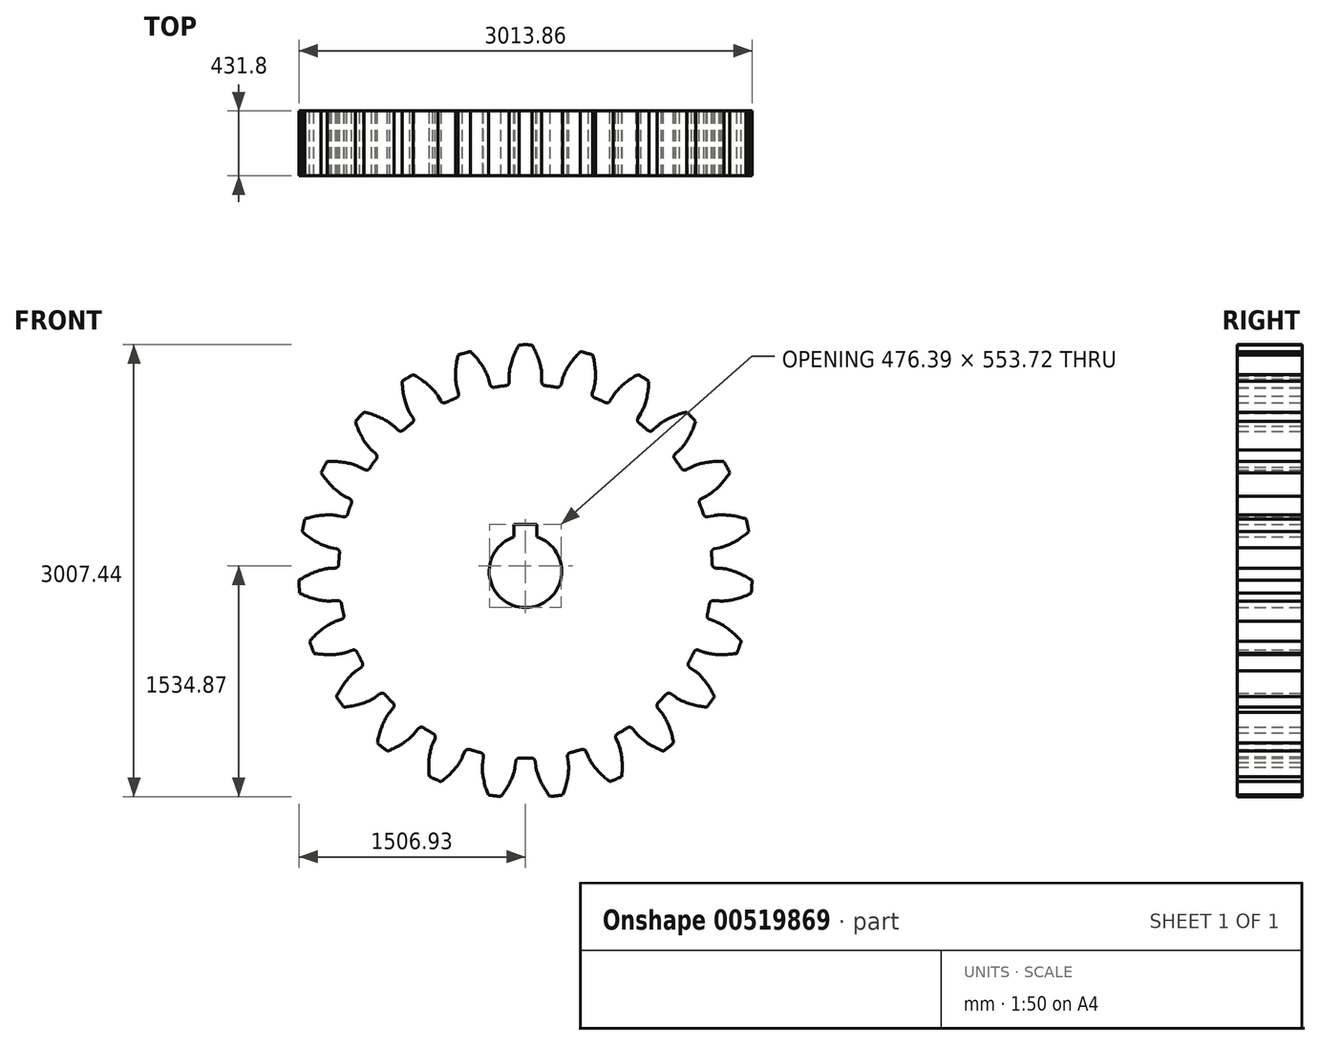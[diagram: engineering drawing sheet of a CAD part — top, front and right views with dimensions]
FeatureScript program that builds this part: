
annotation { "Feature Type Name" : "Feature", "Feature Type Description" : "" }
export const myFeature = defineFeature(function(context is Context, id is Id, definition is map)
    precondition{}
    {
        {
            var Q0;
            Q0=qCreatedBy(makeId("Front.planeOp"),FACE);
            var sketch = newSketch(context, id + "F0", { "sketchPlane" : qUnion([Q0])});
            skCircle(sketch, "E0", {"center": v(0, -4.4) * mm, "radius": 762 * mm});
            skArc(sketch, "E1", {"start": v(-76.2, 224.55) * mm, "mid": v(0, -245.7) * mm, "end": v(76.2, 224.55) * mm});
            skLineSegment(sketch, "E2", {"start": v(-76.2, 224.55) * mm, "end": v(-76.2, 308.01) * mm});
            skLineSegment(sketch, "E3", {"start": v(-76.2, 308.01) * mm, "end": v(76.2, 308.01) * mm});
            skLineSegment(sketch, "E4", {"start": v(76.2, 308.01) * mm, "end": v(76.2, 224.55) * mm});
            skArc(sketch, "E5", {"start": v(169.21, 1226.71) * mm, "mid": v(150.16, 1229.18) * mm, "end": v(131.07, 1231.36) * mm});
            skFitSpline(sketch, "E6", {"points": [v(42.87, 1503.1) * mm, v(49.5, 1490.92) * mm, v(64.07, 1462.34) * mm, v(82.4, 1419.04) * mm, v(96.22, 1376.5) * mm, v(104.12, 1342.62) * mm, v(107.6, 1318.04) * mm, v(108.63, 1303.15) * mm, v(108.4, 1296.54) * mm, v(108.35, 1294.88) * mm]});
            skFitSpline(sketch, "E7", {"points": [v(-42.87, 1503.1) * mm, v(-49.5, 1490.92) * mm, v(-64.07, 1462.34) * mm, v(-82.4, 1419.04) * mm, v(-96.22, 1376.5) * mm, v(-104.12, 1342.62) * mm, v(-107.6, 1318.04) * mm, v(-108.63, 1303.15) * mm, v(-108.4, 1296.54) * mm, v(-108.35, 1294.88) * mm]});
            skLineSegment(sketch, "E8", {"start": v(-108.35, 1294.88) * mm, "end": v(-108.35, 1256.61) * mm});
            skArc(sketch, "E9", {"start": v(-131.07, 1231.36) * mm, "mid": v(-114.87, 1239.63) * mm, "end": v(-108.35, 1256.61) * mm});
            skArc(sketch, "E10", {"start": v(108.35, 1256.61) * mm, "mid": v(114.87, 1239.63) * mm, "end": v(131.07, 1231.36) * mm});
            skLineSegment(sketch, "E11", {"start": v(108.35, 1294.88) * mm, "end": v(108.35, 1256.61) * mm});
            skArc(sketch, "E12", {"start": v(-131.07, 1231.36) * mm, "mid": v(-150.16, 1229.18) * mm, "end": v(-169.21, 1226.71) * mm});
            skArc(sketch, "E13", {"start": v(42.87, 1503.1) * mm, "mid": v(0, 1503.72) * mm, "end": v(-42.87, 1503.1) * mm});
            skFitSpline(sketch, "E14", {"points": [v(-365.44, 1458.77) * mm, v(-355.77, 1448.82) * mm, v(-334.03, 1425.23) * mm, v(-304.7, 1388.48) * mm, v(-279.92, 1351.26) * mm, v(-263.16, 1320.76) * mm, v(-253.19, 1298.03) * mm, v(-248.17, 1283.97) * mm, v(-246.6, 1277.54) * mm, v(-246.2, 1275.94) * mm]});
            skFitSpline(sketch, "E15", {"points": [v(-448, 1435.64) * mm, v(-451.1, 1422.11) * mm, v(-457.42, 1390.66) * mm, v(-463.39, 1344.02) * mm, v(-465.22, 1299.34) * mm, v(-463.69, 1264.58) * mm, v(-460.4, 1239.97) * mm, v(-457.38, 1225.36) * mm, v(-455.38, 1219.05) * mm, v(-454.88, 1217.47) * mm]});
            skLineSegment(sketch, "E16", {"start": v(-454.88, 1217.47) * mm, "end": v(-444.55, 1180.62) * mm});
            skArc(sketch, "E17", {"start": v(-459.62, 1150.17) * mm, "mid": v(-446.25, 1162.5) * mm, "end": v(-444.55, 1180.62) * mm});
            skArc(sketch, "E18", {"start": v(-235.88, 1239.09) * mm, "mid": v(-225.03, 1224.49) * mm, "end": v(-207.2, 1220.9) * mm});
            skLineSegment(sketch, "E19", {"start": v(-246.2, 1275.94) * mm, "end": v(-235.88, 1239.09) * mm});
            skArc(sketch, "E20", {"start": v(-459.62, 1150.17) * mm, "mid": v(-477.41, 1142.92) * mm, "end": v(-495.1, 1135.4) * mm});
            skArc(sketch, "E21", {"start": v(-169.21, 1226.71) * mm, "mid": v(-188.23, 1223.95) * mm, "end": v(-207.2, 1220.9) * mm});
            skArc(sketch, "E22", {"start": v(-365.44, 1458.77) * mm, "mid": v(-406.89, 1447.8) * mm, "end": v(-448, 1435.64) * mm});
            skFitSpline(sketch, "E23", {"points": [v(-746.65, 1305.92) * mm, v(-734.66, 1298.95) * mm, v(-707.35, 1282.1) * mm, v(-669.2, 1254.63) * mm, v(-635.29, 1225.47) * mm, v(-610.93, 1200.62) * mm, v(-595.19, 1181.42) * mm, v(-586.57, 1169.24) * mm, v(-583.32, 1163.47) * mm, v(-582.51, 1162.03) * mm]});
            skFitSpline(sketch, "E24", {"points": [v(-819.9, 1261.37) * mm, v(-819.24, 1247.51) * mm, v(-816.84, 1215.52) * mm, v(-810, 1169) * mm, v(-799.71, 1125.48) * mm, v(-788.86, 1092.42) * mm, v(-779.05, 1069.61) * mm, v(-772.2, 1056.35) * mm, v(-768.58, 1050.82) * mm, v(-767.67, 1049.43) * mm]});
            skLineSegment(sketch, "E25", {"start": v(-767.67, 1049.43) * mm, "end": v(-747.79, 1016.74) * mm});
            skArc(sketch, "E26", {"start": v(-754.07, 983.35) * mm, "mid": v(-744.53, 998.84) * mm, "end": v(-747.79, 1016.74) * mm});
            skArc(sketch, "E27", {"start": v(-562.63, 1129.33) * mm, "mid": v(-548.23, 1118.2) * mm, "end": v(-530.1, 1119.56) * mm});
            skLineSegment(sketch, "E28", {"start": v(-582.51, 1162.03) * mm, "end": v(-562.63, 1129.33) * mm});
            skArc(sketch, "E29", {"start": v(-754.07, 983.35) * mm, "mid": v(-769.25, 971.57) * mm, "end": v(-784.25, 959.57) * mm});
            skArc(sketch, "E30", {"start": v(-495.1, 1135.4) * mm, "mid": v(-512.65, 1127.62) * mm, "end": v(-530.1, 1119.56) * mm});
            skArc(sketch, "E31", {"start": v(-746.65, 1305.92) * mm, "mid": v(-783.6, 1284.16) * mm, "end": v(-819.9, 1261.37) * mm});
            skFitSpline(sketch, "E32", {"points": [v(-1072.49, 1055.88) * mm, v(-1059.05, 1052.4) * mm, v(-1028.22, 1043.55) * mm, v(-984.06, 1027.4) * mm, v(-943.55, 1008.46) * mm, v(-913.39, 991.11) * mm, v(-893.05, 976.87) * mm, v(-881.46, 967.46) * mm, v(-876.78, 962.79) * mm, v(-875.61, 961.62) * mm]});
            skFitSpline(sketch, "E33", {"points": [v(-1131, 993.22) * mm, v(-1126.62, 980.06) * mm, v(-1115.68, 949.9) * mm, v(-1096.55, 906.94) * mm, v(-1074.9, 867.82) * mm, v(-1055.53, 838.92) * mm, v(-1039.93, 819.6) * mm, v(-1029.76, 808.68) * mm, v(-1024.77, 804.33) * mm, v(-1023.52, 803.24) * mm]});
            skLineSegment(sketch, "E34", {"start": v(-1023.52, 803.24) * mm, "end": v(-995.56, 777.12) * mm});
            skArc(sketch, "E35", {"start": v(-992.6, 743.27) * mm, "mid": v(-987.59, 760.76) * mm, "end": v(-995.56, 777.12) * mm});
            skArc(sketch, "E36", {"start": v(-847.64, 935.5) * mm, "mid": v(-830.78, 928.66) * mm, "end": v(-813.68, 934.86) * mm});
            skLineSegment(sketch, "E37", {"start": v(-875.61, 961.62) * mm, "end": v(-847.64, 935.5) * mm});
            skArc(sketch, "E38", {"start": v(-992.6, 743.27) * mm, "mid": v(-1004.04, 727.84) * mm, "end": v(-1015.24, 712.23) * mm});
            skArc(sketch, "E39", {"start": v(-784.25, 959.57) * mm, "mid": v(-799.06, 947.33) * mm, "end": v(-813.68, 934.86) * mm});
            skArc(sketch, "E40", {"start": v(-1072.49, 1055.88) * mm, "mid": v(-1102.2, 1024.97) * mm, "end": v(-1131, 993.22) * mm});
            skFitSpline(sketch, "E41", {"points": [v(-1318.78, 727.21) * mm, v(-1304.9, 727.49) * mm, v(-1272.82, 727.28) * mm, v(-1225.94, 723.64) * mm, v(-1181.83, 716.33) * mm, v(-1148.1, 707.76) * mm, v(-1124.68, 699.54) * mm, v(-1110.99, 693.6) * mm, v(-1105.21, 690.37) * mm, v(-1103.77, 689.56) * mm]});
            skFitSpline(sketch, "E42", {"points": [v(-1358.22, 651.09) * mm, v(-1350.45, 639.6) * mm, v(-1331.78, 613.5) * mm, v(-1301.77, 577.3) * mm, v(-1270.36, 545.47) * mm, v(-1243.91, 522.87) * mm, v(-1223.68, 508.47) * mm, v(-1210.94, 500.7) * mm, v(-1204.96, 497.86) * mm, v(-1203.47, 497.15) * mm]});
            skLineSegment(sketch, "E43", {"start": v(-1203.47, 497.15) * mm, "end": v(-1169.5, 479.54) * mm});
            skArc(sketch, "E44", {"start": v(-1157.52, 447.75) * mm, "mid": v(-1157.4, 465.94) * mm, "end": v(-1169.5, 479.54) * mm});
            skArc(sketch, "E45", {"start": v(-1069.8, 671.95) * mm, "mid": v(-1051.71, 669.92) * mm, "end": v(-1036.91, 680.5) * mm});
            skLineSegment(sketch, "E46", {"start": v(-1103.77, 689.56) * mm, "end": v(-1069.8, 671.95) * mm});
            skArc(sketch, "E47", {"start": v(-1157.52, 447.75) * mm, "mid": v(-1164.37, 429.8) * mm, "end": v(-1170.94, 411.75) * mm});
            skArc(sketch, "E48", {"start": v(-1015.24, 712.23) * mm, "mid": v(-1026.2, 696.45) * mm, "end": v(-1036.91, 680.5) * mm});
            skArc(sketch, "E49", {"start": v(-1318.78, 727.21) * mm, "mid": v(-1339.04, 689.43) * mm, "end": v(-1358.22, 651.09) * mm});
            skFitSpline(sketch, "E50", {"points": [v(-1467.26, 344.28) * mm, v(-1453.98, 348.29) * mm, v(-1423.03, 356.74) * mm, v(-1376.9, 365.88) * mm, v(-1332.45, 370.75) * mm, v(-1297.67, 371.6) * mm, v(-1272.9, 370) * mm, v(-1258.1, 367.98) * mm, v(-1251.68, 366.42) * mm, v(-1250.07, 366.03) * mm]});
            skFitSpline(sketch, "E51", {"points": [v(-1484.7, 260.34) * mm, v(-1474.12, 251.36) * mm, v(-1449.1, 231.28) * mm, v(-1410.44, 204.52) * mm, v(-1371.6, 182.34) * mm, v(-1340.04, 167.7) * mm, v(-1316.68, 159.3) * mm, v(-1302.31, 155.27) * mm, v(-1295.79, 154.14) * mm, v(-1294.16, 153.86) * mm]});
            skLineSegment(sketch, "E52", {"start": v(-1294.16, 153.86) * mm, "end": v(-1256.7, 146.07) * mm});
            skArc(sketch, "E53", {"start": v(-1236.58, 118.68) * mm, "mid": v(-1241.39, 136.23) * mm, "end": v(-1256.7, 146.07) * mm});
            skArc(sketch, "E54", {"start": v(-1212.6, 358.24) * mm, "mid": v(-1194.64, 361.17) * mm, "end": v(-1183.25, 375.35) * mm});
            skLineSegment(sketch, "E55", {"start": v(-1250.07, 366.03) * mm, "end": v(-1212.6, 358.24) * mm});
            skArc(sketch, "E56", {"start": v(-1236.58, 118.68) * mm, "mid": v(-1238.34, 99.55) * mm, "end": v(-1239.8, 80.4) * mm});
            skArc(sketch, "E57", {"start": v(-1170.94, 411.75) * mm, "mid": v(-1177.24, 393.6) * mm, "end": v(-1183.25, 375.35) * mm});
            skArc(sketch, "E58", {"start": v(-1467.26, 344.28) * mm, "mid": v(-1476.58, 302.43) * mm, "end": v(-1484.7, 260.34) * mm});
            skFitSpline(sketch, "E59", {"points": [v(-1506.93, -64.52) * mm, v(-1495.22, -57.07) * mm, v(-1467.7, -40.58) * mm, v(-1425.75, -19.33) * mm, v(-1384.26, -2.65) * mm, v(-1351, 7.55) * mm, v(-1326.7, 12.7) * mm, v(-1311.92, 14.74) * mm, v(-1305.3, 14.97) * mm, v(-1303.66, 15.03) * mm]});
            skFitSpline(sketch, "E60", {"points": [v(-1501.08, -150.05) * mm, v(-1488.46, -155.83) * mm, v(-1458.95, -168.42) * mm, v(-1414.5, -183.76) * mm, v(-1371.13, -194.64) * mm, v(-1336.79, -200.21) * mm, v(-1312.02, -202) * mm, v(-1297.1, -202.02) * mm, v(-1290.51, -201.34) * mm, v(-1288.87, -201.17) * mm]});
            skLineSegment(sketch, "E61", {"start": v(-1288.87, -201.17) * mm, "end": v(-1250.69, -198.56) * mm});
            skArc(sketch, "E62", {"start": v(-1223.94, -219.5) * mm, "mid": v(-1233.3, -203.9) * mm, "end": v(-1250.69, -198.56) * mm});
            skArc(sketch, "E63", {"start": v(-1265.48, 17.64) * mm, "mid": v(-1248.97, 25.3) * mm, "end": v(-1241.83, 42.03) * mm});
            skLineSegment(sketch, "E64", {"start": v(-1303.66, 15.03) * mm, "end": v(-1265.48, 17.64) * mm});
            skArc(sketch, "E65", {"start": v(-1223.94, -219.5) * mm, "mid": v(-1220.47, -238.4) * mm, "end": v(-1216.7, -257.24) * mm});
            skArc(sketch, "E66", {"start": v(-1239.8, 80.4) * mm, "mid": v(-1240.96, 61.22) * mm, "end": v(-1241.83, 42.03) * mm});
            skArc(sketch, "E67", {"start": v(-1506.93, -64.52) * mm, "mid": v(-1504.6, -107.32) * mm, "end": v(-1501.08, -150.05) * mm});
            skFitSpline(sketch, "E68", {"points": [v(-1434.83, -468.85) * mm, v(-1425.56, -458.52) * mm, v(-1403.51, -435.22) * mm, v(-1368.85, -403.44) * mm, v(-1333.4, -376.18) * mm, v(-1304.12, -357.39) * mm, v(-1282.12, -345.88) * mm, v(-1268.44, -339.92) * mm, v(-1262.13, -337.92) * mm, v(-1260.56, -337.42) * mm]});
            skFitSpline(sketch, "E69", {"points": [v(-1406.12, -549.64) * mm, v(-1392.41, -551.8) * mm, v(-1360.6, -555.96) * mm, v(-1313.66, -558.74) * mm, v(-1268.96, -557.5) * mm, v(-1234.39, -553.61) * mm, v(-1210.06, -548.65) * mm, v(-1195.68, -544.64) * mm, v(-1189.52, -542.22) * mm, v(-1187.98, -541.6) * mm]});
            skLineSegment(sketch, "E70", {"start": v(-1187.98, -541.6) * mm, "end": v(-1151.93, -528.8) * mm});
            skArc(sketch, "E71", {"start": v(-1120.52, -541.74) * mm, "mid": v(-1133.74, -529.24) * mm, "end": v(-1151.93, -528.8) * mm});
            skArc(sketch, "E72", {"start": v(-1224.5, -324.6) * mm, "mid": v(-1210.67, -312.77) * mm, "end": v(-1208.3, -294.73) * mm});
            skLineSegment(sketch, "E73", {"start": v(-1260.56, -337.42) * mm, "end": v(-1224.5, -324.6) * mm});
            skArc(sketch, "E74", {"start": v(-1120.52, -541.74) * mm, "mid": v(-1112.08, -559) * mm, "end": v(-1103.37, -576.13) * mm});
            skArc(sketch, "E75", {"start": v(-1216.7, -257.24) * mm, "mid": v(-1212.65, -276.02) * mm, "end": v(-1208.3, -294.73) * mm});
            skArc(sketch, "E76", {"start": v(-1434.83, -468.85) * mm, "mid": v(-1421.05, -509.45) * mm, "end": v(-1406.12, -549.64) * mm});
            skFitSpline(sketch, "E77", {"points": [v(-1256.32, -838.74) * mm, v(-1250.18, -826.3) * mm, v(-1235.23, -797.9) * mm, v(-1210.43, -757.96) * mm, v(-1183.65, -722.15) * mm, v(-1160.53, -696.15) * mm, v(-1142.45, -679.13) * mm, v(-1130.88, -669.7) * mm, v(-1125.35, -666.07) * mm, v(-1123.97, -665.16) * mm]});
            skFitSpline(sketch, "E78", {"points": [v(-1206.87, -908.78) * mm, v(-1193.1, -907.17) * mm, v(-1161.34, -902.6) * mm, v(-1115.39, -892.6) * mm, v(-1072.68, -879.36) * mm, v(-1040.44, -866.28) * mm, v(-1018.35, -854.94) * mm, v(-1005.6, -847.2) * mm, v(-1000.31, -843.2) * mm, v(-999, -842.2) * mm]});
            skLineSegment(sketch, "E79", {"start": v(-999, -842.2) * mm, "end": v(-967.73, -820.13) * mm});
            skArc(sketch, "E80", {"start": v(-934, -824.13) * mm, "mid": v(-950.1, -815.66) * mm, "end": v(-967.73, -820.13) * mm});
            skArc(sketch, "E81", {"start": v(-1092.7, -643.1) * mm, "mid": v(-1082.58, -627.97) * mm, "end": v(-1085.17, -609.96) * mm});
            skLineSegment(sketch, "E82", {"start": v(-1123.97, -665.16) * mm, "end": v(-1092.7, -643.1) * mm});
            skArc(sketch, "E83", {"start": v(-934, -824.13) * mm, "mid": v(-921.2, -838.47) * mm, "end": v(-908.2, -852.61) * mm});
            skArc(sketch, "E84", {"start": v(-1103.37, -576.13) * mm, "mid": v(-1094.4, -593.12) * mm, "end": v(-1085.17, -609.96) * mm});
            skArc(sketch, "E85", {"start": v(-1256.32, -838.74) * mm, "mid": v(-1232.1, -874.11) * mm, "end": v(-1206.87, -908.78) * mm});
            skFitSpline(sketch, "E86", {"points": [v(-984.63, -1146.75) * mm, v(-982.08, -1133.11) * mm, v(-975.35, -1101.74) * mm, v(-962.24, -1056.58) * mm, v(-946.12, -1014.88) * mm, v(-930.86, -983.6) * mm, v(-918.04, -962.34) * mm, v(-909.45, -950.14) * mm, v(-905.1, -945.15) * mm, v(-904.02, -943.9) * mm]});
            skFitSpline(sketch, "E87", {"points": [v(-918.12, -1200.86) * mm, v(-905.29, -1195.59) * mm, v(-875.94, -1182.61) * mm, v(-834.4, -1160.6) * mm, v(-796.84, -1136.32) * mm, v(-769.33, -1115.02) * mm, v(-751.12, -1098.14) * mm, v(-740.92, -1087.25) * mm, v(-736.92, -1081.98) * mm, v(-735.92, -1080.66) * mm]});
            skLineSegment(sketch, "E88", {"start": v(-735.92, -1080.66) * mm, "end": v(-711.76, -1050.98) * mm});
            skArc(sketch, "E89", {"start": v(-678.2, -1045.72) * mm, "mid": v(-696, -1041.91) * mm, "end": v(-711.76, -1050.98) * mm});
            skArc(sketch, "E90", {"start": v(-879.87, -914.22) * mm, "mid": v(-874.2, -896.93) * mm, "end": v(-881.55, -880.28) * mm});
            skLineSegment(sketch, "E91", {"start": v(-904.02, -943.9) * mm, "end": v(-879.87, -914.22) * mm});
            skArc(sketch, "E92", {"start": v(-678.2, -1045.72) * mm, "mid": v(-662.02, -1056.08) * mm, "end": v(-645.68, -1066.19) * mm});
            skArc(sketch, "E93", {"start": v(-908.2, -852.61) * mm, "mid": v(-894.99, -866.55) * mm, "end": v(-881.55, -880.28) * mm});
            skArc(sketch, "E94", {"start": v(-984.63, -1146.75) * mm, "mid": v(-951.76, -1174.28) * mm, "end": v(-918.12, -1200.86) * mm});
            skFitSpline(sketch, "E95", {"points": [v(-639.91, -1370.04) * mm, v(-641.14, -1356.22) * mm, v(-643.12, -1324.2) * mm, v(-642.68, -1277.17) * mm, v(-638.41, -1232.66) * mm, v(-632.16, -1198.44) * mm, v(-625.55, -1174.5) * mm, v(-620.57, -1160.44) * mm, v(-617.73, -1154.46) * mm, v(-617.02, -1152.96) * mm]});
            skFitSpline(sketch, "E96", {"points": [v(-561.28, -1404.2) * mm, v(-550.34, -1395.66) * mm, v(-525.59, -1375.25) * mm, v(-491.52, -1342.83) * mm, v(-461.9, -1309.33) * mm, v(-441.16, -1281.4) * mm, v(-428.17, -1260.23) * mm, v(-421.3, -1247) * mm, v(-418.86, -1240.84) * mm, v(-418.26, -1239.3) * mm]});
            skLineSegment(sketch, "E97", {"start": v(-418.26, -1239.3) * mm, "end": v(-403, -1204.2) * mm});
            skArc(sketch, "E98", {"start": v(-372.1, -1190.08) * mm, "mid": v(-390.27, -1191.21) * mm, "end": v(-403, -1204.2) * mm});
            skArc(sketch, "E99", {"start": v(-601.77, -1117.86) * mm, "mid": v(-600.98, -1099.69) * mm, "end": v(-612.55, -1085.64) * mm});
            skLineSegment(sketch, "E100", {"start": v(-617.02, -1152.96) * mm, "end": v(-601.77, -1117.86) * mm});
            skArc(sketch, "E101", {"start": v(-372.1, -1190.08) * mm, "mid": v(-353.73, -1195.7) * mm, "end": v(-335.28, -1201.02) * mm});
            skArc(sketch, "E102", {"start": v(-645.68, -1066.19) * mm, "mid": v(-629.2, -1076.04) * mm, "end": v(-612.55, -1085.64) * mm});
            skArc(sketch, "E103", {"start": v(-639.91, -1370.04) * mm, "mid": v(-600.84, -1387.68) * mm, "end": v(-561.28, -1404.2) * mm});
            skFitSpline(sketch, "E104", {"points": [v(-247.74, -1492.04) * mm, v(-252.65, -1479.07) * mm, v(-263.2, -1448.76) * mm, v(-275.46, -1403.37) * mm, v(-283.36, -1359.36) * mm, v(-286.57, -1324.71) * mm, v(-286.67, -1299.88) * mm, v(-285.67, -1285) * mm, v(-284.54, -1278.47) * mm, v(-284.26, -1276.84) * mm]});
            skFitSpline(sketch, "E105", {"points": [v(-162.8, -1503.72) * mm, v(-154.58, -1492.55) * mm, v(-136.25, -1466.21) * mm, v(-112.19, -1425.81) * mm, v(-92.71, -1385.56) * mm, v(-80.27, -1353.07) * mm, v(-73.48, -1329.18) * mm, v(-70.43, -1314.58) * mm, v(-69.75, -1308) * mm, v(-69.58, -1306.35) * mm]});
            skLineSegment(sketch, "E106", {"start": v(-69.58, -1306.35) * mm, "end": v(-64.37, -1268.44) * mm});
            skArc(sketch, "E107", {"start": v(-38.42, -1246.5) * mm, "mid": v(-55.6, -1252.5) * mm, "end": v(-64.37, -1268.44) * mm});
            skArc(sketch, "E108", {"start": v(-279.05, -1238.93) * mm, "mid": v(-283.2, -1221.21) * mm, "end": v(-298.12, -1210.81) * mm});
            skLineSegment(sketch, "E109", {"start": v(-284.26, -1276.84) * mm, "end": v(-279.05, -1238.93) * mm});
            skArc(sketch, "E110", {"start": v(-38.42, -1246.5) * mm, "mid": v(-19.21, -1246.95) * mm, "end": v(0, -1247.1) * mm});
            skArc(sketch, "E111", {"start": v(-335.28, -1201.02) * mm, "mid": v(-316.74, -1206.06) * mm, "end": v(-298.12, -1210.81) * mm});
            skArc(sketch, "E112", {"start": v(-247.74, -1492.04) * mm, "mid": v(-205.36, -1498.48) * mm, "end": v(-162.8, -1503.72) * mm});
            skFitSpline(sketch, "E113", {"points": [v(162.8, -1503.72) * mm, v(154.58, -1492.55) * mm, v(136.25, -1466.21) * mm, v(112.19, -1425.81) * mm, v(92.71, -1385.56) * mm, v(80.27, -1353.07) * mm, v(73.48, -1329.18) * mm, v(70.43, -1314.58) * mm, v(69.75, -1308) * mm, v(69.58, -1306.35) * mm]});
            skFitSpline(sketch, "E114", {"points": [v(247.74, -1492.04) * mm, v(252.65, -1479.07) * mm, v(263.2, -1448.76) * mm, v(275.46, -1403.37) * mm, v(283.36, -1359.36) * mm, v(286.57, -1324.71) * mm, v(286.67, -1299.88) * mm, v(285.67, -1285) * mm, v(284.54, -1278.47) * mm, v(284.26, -1276.84) * mm]});
            skLineSegment(sketch, "E115", {"start": v(284.26, -1276.84) * mm, "end": v(279.05, -1238.93) * mm});
            skArc(sketch, "E116", {"start": v(298.12, -1210.81) * mm, "mid": v(283.2, -1221.21) * mm, "end": v(279.05, -1238.93) * mm});
            skArc(sketch, "E117", {"start": v(64.37, -1268.44) * mm, "mid": v(55.6, -1252.5) * mm, "end": v(38.42, -1246.5) * mm});
            skLineSegment(sketch, "E118", {"start": v(69.58, -1306.35) * mm, "end": v(64.37, -1268.44) * mm});
            skArc(sketch, "E119", {"start": v(298.12, -1210.81) * mm, "mid": v(316.74, -1206.06) * mm, "end": v(335.28, -1201.02) * mm});
            skArc(sketch, "E120", {"start": v(0, -1247.1) * mm, "mid": v(19.21, -1246.95) * mm, "end": v(38.42, -1246.5) * mm});
            skArc(sketch, "E121", {"start": v(162.8, -1503.72) * mm, "mid": v(205.36, -1498.48) * mm, "end": v(247.74, -1492.04) * mm});
            skFitSpline(sketch, "E122", {"points": [v(561.28, -1404.2) * mm, v(550.34, -1395.66) * mm, v(525.59, -1375.25) * mm, v(491.52, -1342.83) * mm, v(461.9, -1309.33) * mm, v(441.16, -1281.4) * mm, v(428.17, -1260.23) * mm, v(421.3, -1247) * mm, v(418.86, -1240.84) * mm, v(418.26, -1239.3) * mm]});
            skFitSpline(sketch, "E123", {"points": [v(639.91, -1370.04) * mm, v(641.14, -1356.22) * mm, v(643.12, -1324.2) * mm, v(642.68, -1277.17) * mm, v(638.41, -1232.66) * mm, v(632.16, -1198.44) * mm, v(625.55, -1174.5) * mm, v(620.57, -1160.44) * mm, v(617.73, -1154.46) * mm, v(617.02, -1152.96) * mm]});
            skLineSegment(sketch, "E124", {"start": v(617.02, -1152.96) * mm, "end": v(601.77, -1117.86) * mm});
            skArc(sketch, "E125", {"start": v(612.55, -1085.64) * mm, "mid": v(600.98, -1099.69) * mm, "end": v(601.77, -1117.86) * mm});
            skArc(sketch, "E126", {"start": v(403, -1204.2) * mm, "mid": v(390.27, -1191.21) * mm, "end": v(372.1, -1190.08) * mm});
            skLineSegment(sketch, "E127", {"start": v(418.26, -1239.3) * mm, "end": v(403, -1204.2) * mm});
            skArc(sketch, "E128", {"start": v(612.55, -1085.64) * mm, "mid": v(629.2, -1076.04) * mm, "end": v(645.68, -1066.19) * mm});
            skArc(sketch, "E129", {"start": v(335.28, -1201.02) * mm, "mid": v(353.73, -1195.7) * mm, "end": v(372.1, -1190.08) * mm});
            skArc(sketch, "E130", {"start": v(561.28, -1404.2) * mm, "mid": v(600.84, -1387.68) * mm, "end": v(639.91, -1370.04) * mm});
            skFitSpline(sketch, "E131", {"points": [v(918.12, -1200.86) * mm, v(905.29, -1195.59) * mm, v(875.94, -1182.61) * mm, v(834.4, -1160.6) * mm, v(796.84, -1136.32) * mm, v(769.33, -1115.02) * mm, v(751.12, -1098.14) * mm, v(740.92, -1087.25) * mm, v(736.92, -1081.98) * mm, v(735.92, -1080.66) * mm]});
            skFitSpline(sketch, "E132", {"points": [v(984.63, -1146.75) * mm, v(982.08, -1133.11) * mm, v(975.35, -1101.74) * mm, v(962.24, -1056.58) * mm, v(946.12, -1014.88) * mm, v(930.86, -983.6) * mm, v(918.04, -962.34) * mm, v(909.45, -950.14) * mm, v(905.1, -945.15) * mm, v(904.02, -943.9) * mm]});
            skLineSegment(sketch, "E133", {"start": v(904.02, -943.9) * mm, "end": v(879.87, -914.22) * mm});
            skArc(sketch, "E134", {"start": v(881.55, -880.28) * mm, "mid": v(874.2, -896.93) * mm, "end": v(879.87, -914.22) * mm});
            skArc(sketch, "E135", {"start": v(711.76, -1050.98) * mm, "mid": v(696, -1041.91) * mm, "end": v(678.2, -1045.72) * mm});
            skLineSegment(sketch, "E136", {"start": v(735.92, -1080.66) * mm, "end": v(711.76, -1050.98) * mm});
            skArc(sketch, "E137", {"start": v(881.55, -880.28) * mm, "mid": v(894.99, -866.55) * mm, "end": v(908.2, -852.61) * mm});
            skArc(sketch, "E138", {"start": v(645.68, -1066.19) * mm, "mid": v(662.02, -1056.08) * mm, "end": v(678.2, -1045.72) * mm});
            skArc(sketch, "E139", {"start": v(918.12, -1200.86) * mm, "mid": v(951.76, -1174.28) * mm, "end": v(984.63, -1146.75) * mm});
            skFitSpline(sketch, "E140", {"points": [v(1206.87, -908.78) * mm, v(1193.1, -907.17) * mm, v(1161.34, -902.6) * mm, v(1115.39, -892.6) * mm, v(1072.68, -879.36) * mm, v(1040.44, -866.28) * mm, v(1018.35, -854.94) * mm, v(1005.6, -847.2) * mm, v(1000.31, -843.2) * mm, v(999, -842.2) * mm]});
            skFitSpline(sketch, "E141", {"points": [v(1256.32, -838.74) * mm, v(1250.18, -826.3) * mm, v(1235.23, -797.9) * mm, v(1210.43, -757.96) * mm, v(1183.65, -722.15) * mm, v(1160.53, -696.15) * mm, v(1142.45, -679.13) * mm, v(1130.88, -669.7) * mm, v(1125.35, -666.07) * mm, v(1123.97, -665.16) * mm]});
            skLineSegment(sketch, "E142", {"start": v(1123.97, -665.16) * mm, "end": v(1092.7, -643.1) * mm});
            skArc(sketch, "E143", {"start": v(1085.17, -609.96) * mm, "mid": v(1082.58, -627.97) * mm, "end": v(1092.7, -643.1) * mm});
            skArc(sketch, "E144", {"start": v(967.73, -820.13) * mm, "mid": v(950.1, -815.66) * mm, "end": v(934, -824.13) * mm});
            skLineSegment(sketch, "E145", {"start": v(999, -842.2) * mm, "end": v(967.73, -820.13) * mm});
            skArc(sketch, "E146", {"start": v(1085.17, -609.96) * mm, "mid": v(1094.4, -593.12) * mm, "end": v(1103.37, -576.13) * mm});
            skArc(sketch, "E147", {"start": v(908.2, -852.61) * mm, "mid": v(921.2, -838.47) * mm, "end": v(934, -824.13) * mm});
            skArc(sketch, "E148", {"start": v(1206.87, -908.78) * mm, "mid": v(1232.1, -874.11) * mm, "end": v(1256.32, -838.74) * mm});
            skFitSpline(sketch, "E149", {"points": [v(1406.12, -549.64) * mm, v(1392.41, -551.8) * mm, v(1360.6, -555.96) * mm, v(1313.66, -558.74) * mm, v(1268.96, -557.5) * mm, v(1234.39, -553.61) * mm, v(1210.06, -548.65) * mm, v(1195.68, -544.64) * mm, v(1189.52, -542.22) * mm, v(1187.98, -541.6) * mm]});
            skFitSpline(sketch, "E150", {"points": [v(1434.83, -468.85) * mm, v(1425.56, -458.52) * mm, v(1403.51, -435.22) * mm, v(1368.85, -403.44) * mm, v(1333.4, -376.18) * mm, v(1304.12, -357.39) * mm, v(1282.12, -345.88) * mm, v(1268.44, -339.92) * mm, v(1262.13, -337.92) * mm, v(1260.56, -337.42) * mm]});
            skLineSegment(sketch, "E151", {"start": v(1260.56, -337.42) * mm, "end": v(1224.5, -324.6) * mm});
            skArc(sketch, "E152", {"start": v(1208.3, -294.73) * mm, "mid": v(1210.67, -312.77) * mm, "end": v(1224.5, -324.6) * mm});
            skArc(sketch, "E153", {"start": v(1151.93, -528.8) * mm, "mid": v(1133.74, -529.24) * mm, "end": v(1120.52, -541.74) * mm});
            skLineSegment(sketch, "E154", {"start": v(1187.98, -541.6) * mm, "end": v(1151.93, -528.8) * mm});
            skArc(sketch, "E155", {"start": v(1208.3, -294.73) * mm, "mid": v(1212.65, -276.02) * mm, "end": v(1216.7, -257.24) * mm});
            skArc(sketch, "E156", {"start": v(1103.37, -576.13) * mm, "mid": v(1112.08, -559) * mm, "end": v(1120.52, -541.74) * mm});
            skArc(sketch, "E157", {"start": v(1406.12, -549.64) * mm, "mid": v(1421.05, -509.45) * mm, "end": v(1434.83, -468.85) * mm});
            skFitSpline(sketch, "E158", {"points": [v(1501.08, -150.05) * mm, v(1488.46, -155.83) * mm, v(1458.95, -168.42) * mm, v(1414.5, -183.76) * mm, v(1371.13, -194.64) * mm, v(1336.79, -200.21) * mm, v(1312.02, -202) * mm, v(1297.1, -202.02) * mm, v(1290.51, -201.34) * mm, v(1288.87, -201.17) * mm]});
            skFitSpline(sketch, "E159", {"points": [v(1506.93, -64.52) * mm, v(1495.22, -57.07) * mm, v(1467.7, -40.58) * mm, v(1425.75, -19.33) * mm, v(1384.26, -2.65) * mm, v(1351, 7.55) * mm, v(1326.7, 12.7) * mm, v(1311.92, 14.74) * mm, v(1305.3, 14.97) * mm, v(1303.66, 15.03) * mm]});
            skLineSegment(sketch, "E160", {"start": v(1303.66, 15.03) * mm, "end": v(1265.48, 17.64) * mm});
            skArc(sketch, "E161", {"start": v(1241.83, 42.03) * mm, "mid": v(1248.97, 25.3) * mm, "end": v(1265.48, 17.64) * mm});
            skArc(sketch, "E162", {"start": v(1250.69, -198.56) * mm, "mid": v(1233.3, -203.9) * mm, "end": v(1223.94, -219.5) * mm});
            skLineSegment(sketch, "E163", {"start": v(1288.87, -201.17) * mm, "end": v(1250.69, -198.56) * mm});
            skArc(sketch, "E164", {"start": v(1241.83, 42.03) * mm, "mid": v(1240.96, 61.22) * mm, "end": v(1239.8, 80.4) * mm});
            skArc(sketch, "E165", {"start": v(1216.7, -257.24) * mm, "mid": v(1220.47, -238.4) * mm, "end": v(1223.94, -219.5) * mm});
            skArc(sketch, "E166", {"start": v(1501.08, -150.05) * mm, "mid": v(1504.6, -107.32) * mm, "end": v(1506.93, -64.52) * mm});
            skFitSpline(sketch, "E167", {"points": [v(1484.7, 260.34) * mm, v(1474.12, 251.36) * mm, v(1449.1, 231.28) * mm, v(1410.44, 204.52) * mm, v(1371.6, 182.34) * mm, v(1340.04, 167.7) * mm, v(1316.68, 159.3) * mm, v(1302.31, 155.27) * mm, v(1295.79, 154.14) * mm, v(1294.16, 153.86) * mm]});
            skFitSpline(sketch, "E168", {"points": [v(1467.26, 344.28) * mm, v(1453.98, 348.29) * mm, v(1423.03, 356.74) * mm, v(1376.9, 365.88) * mm, v(1332.45, 370.75) * mm, v(1297.67, 371.6) * mm, v(1272.9, 370) * mm, v(1258.1, 367.98) * mm, v(1251.68, 366.42) * mm, v(1250.07, 366.03) * mm]});
            skLineSegment(sketch, "E169", {"start": v(1250.07, 366.03) * mm, "end": v(1212.6, 358.24) * mm});
            skArc(sketch, "E170", {"start": v(1183.25, 375.35) * mm, "mid": v(1194.64, 361.17) * mm, "end": v(1212.6, 358.24) * mm});
            skArc(sketch, "E171", {"start": v(1256.7, 146.07) * mm, "mid": v(1241.39, 136.23) * mm, "end": v(1236.58, 118.68) * mm});
            skLineSegment(sketch, "E172", {"start": v(1294.16, 153.86) * mm, "end": v(1256.7, 146.07) * mm});
            skArc(sketch, "E173", {"start": v(1183.25, 375.35) * mm, "mid": v(1177.24, 393.6) * mm, "end": v(1170.94, 411.75) * mm});
            skArc(sketch, "E174", {"start": v(1239.8, 80.4) * mm, "mid": v(1238.34, 99.55) * mm, "end": v(1236.58, 118.68) * mm});
            skArc(sketch, "E175", {"start": v(1484.7, 260.34) * mm, "mid": v(1476.58, 302.43) * mm, "end": v(1467.26, 344.28) * mm});
            skFitSpline(sketch, "E176", {"points": [v(1358.22, 651.09) * mm, v(1350.45, 639.6) * mm, v(1331.78, 613.5) * mm, v(1301.77, 577.3) * mm, v(1270.36, 545.47) * mm, v(1243.91, 522.87) * mm, v(1223.68, 508.47) * mm, v(1210.94, 500.7) * mm, v(1204.96, 497.86) * mm, v(1203.47, 497.15) * mm]});
            skFitSpline(sketch, "E177", {"points": [v(1318.78, 727.21) * mm, v(1304.9, 727.49) * mm, v(1272.82, 727.28) * mm, v(1225.94, 723.64) * mm, v(1181.83, 716.33) * mm, v(1148.1, 707.76) * mm, v(1124.68, 699.54) * mm, v(1110.99, 693.6) * mm, v(1105.21, 690.37) * mm, v(1103.77, 689.56) * mm]});
            skLineSegment(sketch, "E178", {"start": v(1103.77, 689.56) * mm, "end": v(1069.8, 671.95) * mm});
            skArc(sketch, "E179", {"start": v(1036.91, 680.5) * mm, "mid": v(1051.71, 669.92) * mm, "end": v(1069.8, 671.95) * mm});
            skArc(sketch, "E180", {"start": v(1169.5, 479.54) * mm, "mid": v(1157.4, 465.94) * mm, "end": v(1157.52, 447.75) * mm});
            skLineSegment(sketch, "E181", {"start": v(1203.47, 497.15) * mm, "end": v(1169.5, 479.54) * mm});
            skArc(sketch, "E182", {"start": v(1036.91, 680.5) * mm, "mid": v(1026.2, 696.45) * mm, "end": v(1015.24, 712.23) * mm});
            skArc(sketch, "E183", {"start": v(1170.94, 411.75) * mm, "mid": v(1164.37, 429.8) * mm, "end": v(1157.52, 447.75) * mm});
            skArc(sketch, "E184", {"start": v(1358.22, 651.09) * mm, "mid": v(1339.04, 689.43) * mm, "end": v(1318.78, 727.21) * mm});
            skFitSpline(sketch, "E185", {"points": [v(1131, 993.22) * mm, v(1126.62, 980.06) * mm, v(1115.68, 949.9) * mm, v(1096.55, 906.94) * mm, v(1074.9, 867.82) * mm, v(1055.53, 838.92) * mm, v(1039.93, 819.6) * mm, v(1029.76, 808.68) * mm, v(1024.77, 804.33) * mm, v(1023.52, 803.24) * mm]});
            skFitSpline(sketch, "E186", {"points": [v(1072.49, 1055.88) * mm, v(1059.05, 1052.4) * mm, v(1028.22, 1043.55) * mm, v(984.06, 1027.4) * mm, v(943.55, 1008.46) * mm, v(913.39, 991.11) * mm, v(893.05, 976.87) * mm, v(881.46, 967.46) * mm, v(876.78, 962.79) * mm, v(875.61, 961.62) * mm]});
            skLineSegment(sketch, "E187", {"start": v(875.61, 961.62) * mm, "end": v(847.64, 935.5) * mm});
            skArc(sketch, "E188", {"start": v(813.68, 934.86) * mm, "mid": v(830.78, 928.66) * mm, "end": v(847.64, 935.5) * mm});
            skArc(sketch, "E189", {"start": v(995.56, 777.12) * mm, "mid": v(987.59, 760.76) * mm, "end": v(992.6, 743.27) * mm});
            skLineSegment(sketch, "E190", {"start": v(1023.52, 803.24) * mm, "end": v(995.56, 777.12) * mm});
            skArc(sketch, "E191", {"start": v(813.68, 934.86) * mm, "mid": v(799.06, 947.33) * mm, "end": v(784.25, 959.57) * mm});
            skArc(sketch, "E192", {"start": v(1015.24, 712.23) * mm, "mid": v(1004.04, 727.84) * mm, "end": v(992.6, 743.27) * mm});
            skArc(sketch, "E193", {"start": v(1131, 993.22) * mm, "mid": v(1102.2, 1024.97) * mm, "end": v(1072.49, 1055.88) * mm});
            skFitSpline(sketch, "E194", {"points": [v(819.9, 1261.37) * mm, v(819.24, 1247.51) * mm, v(816.84, 1215.52) * mm, v(810, 1169) * mm, v(799.71, 1125.48) * mm, v(788.86, 1092.42) * mm, v(779.05, 1069.61) * mm, v(772.2, 1056.35) * mm, v(768.58, 1050.82) * mm, v(767.67, 1049.43) * mm]});
            skFitSpline(sketch, "E195", {"points": [v(746.65, 1305.92) * mm, v(734.66, 1298.95) * mm, v(707.35, 1282.1) * mm, v(669.2, 1254.63) * mm, v(635.29, 1225.47) * mm, v(610.93, 1200.62) * mm, v(595.19, 1181.42) * mm, v(586.57, 1169.24) * mm, v(583.32, 1163.47) * mm, v(582.51, 1162.03) * mm]});
            skLineSegment(sketch, "E196", {"start": v(582.51, 1162.03) * mm, "end": v(562.63, 1129.33) * mm});
            skArc(sketch, "E197", {"start": v(530.1, 1119.56) * mm, "mid": v(548.23, 1118.2) * mm, "end": v(562.63, 1129.33) * mm});
            skArc(sketch, "E198", {"start": v(747.79, 1016.74) * mm, "mid": v(744.53, 998.84) * mm, "end": v(754.07, 983.35) * mm});
            skLineSegment(sketch, "E199", {"start": v(767.67, 1049.43) * mm, "end": v(747.79, 1016.74) * mm});
            skArc(sketch, "E200", {"start": v(530.1, 1119.56) * mm, "mid": v(512.65, 1127.62) * mm, "end": v(495.1, 1135.4) * mm});
            skArc(sketch, "E201", {"start": v(784.25, 959.57) * mm, "mid": v(769.25, 971.57) * mm, "end": v(754.07, 983.35) * mm});
            skArc(sketch, "E202", {"start": v(819.9, 1261.37) * mm, "mid": v(783.6, 1284.16) * mm, "end": v(746.65, 1305.92) * mm});
            skFitSpline(sketch, "E203", {"points": [v(448, 1435.64) * mm, v(451.1, 1422.11) * mm, v(457.42, 1390.66) * mm, v(463.39, 1344.02) * mm, v(465.22, 1299.34) * mm, v(463.69, 1264.58) * mm, v(460.4, 1239.97) * mm, v(457.38, 1225.36) * mm, v(455.38, 1219.05) * mm, v(454.88, 1217.47) * mm]});
            skFitSpline(sketch, "E204", {"points": [v(365.44, 1458.77) * mm, v(355.77, 1448.82) * mm, v(334.03, 1425.23) * mm, v(304.7, 1388.48) * mm, v(279.92, 1351.26) * mm, v(263.16, 1320.76) * mm, v(253.19, 1298.03) * mm, v(248.17, 1283.97) * mm, v(246.6, 1277.54) * mm, v(246.2, 1275.94) * mm]});
            skLineSegment(sketch, "E205", {"start": v(246.2, 1275.94) * mm, "end": v(235.88, 1239.09) * mm});
            skArc(sketch, "E206", {"start": v(207.2, 1220.9) * mm, "mid": v(225.03, 1224.49) * mm, "end": v(235.88, 1239.09) * mm});
            skArc(sketch, "E207", {"start": v(444.55, 1180.62) * mm, "mid": v(446.25, 1162.5) * mm, "end": v(459.62, 1150.17) * mm});
            skLineSegment(sketch, "E208", {"start": v(454.88, 1217.47) * mm, "end": v(444.55, 1180.62) * mm});
            skArc(sketch, "E209", {"start": v(207.2, 1220.9) * mm, "mid": v(188.23, 1223.95) * mm, "end": v(169.21, 1226.71) * mm});
            skArc(sketch, "E210", {"start": v(495.1, 1135.4) * mm, "mid": v(477.41, 1142.92) * mm, "end": v(459.62, 1150.17) * mm});
            skArc(sketch, "E211", {"start": v(448, 1435.64) * mm, "mid": v(406.89, 1447.8) * mm, "end": v(365.44, 1458.77) * mm});
            skSolve(sketch);
        }
        {
            var Q0;
            Q0=makeQuery(id+"F0.imprint","IMPRINT",FACE,{"disambiguationData":[TD([[makeQuery(id+"F0.imprint","IMPRINT",EDGE,{"derivedFrom":sQuery(id+"F0.wireOp",EDGE,"E0")}),1.0]])]});
            var Q1;
            Q1=makeQuery(id+"F0.imprint","IMPRINT",FACE,{"disambiguationData":[TD([[makeQuery(id+"F0.imprint","IMPRINT",EDGE,{"derivedFrom":sQuery(id+"F0.wireOp",EDGE,"E0")}),-1.0]])]});
            extrude(context, id + "F1", {"entities" : qUnion([Q0, Q1]), "depth" : 431.8 * mm, "offsetDistance" : 25 * mm});
        }
    });
